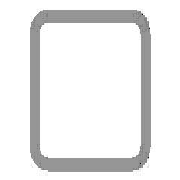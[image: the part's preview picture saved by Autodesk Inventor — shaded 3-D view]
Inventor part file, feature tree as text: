
AUTODESK INVENTOR PART (.ipt)
format: ipt  version: 2025 (Build 290162010, 162A)  size: 133,120 bytes
history: native  units: mm (DEFAULTED — no unit token found)
features: other x4, sketch x1, plane x1
ambient origin geometry x8: Origin, YZ Plane, XZ Plane, XY Plane, X Axis, Y Axis, Z Axis, Center Point
bodies: Solid1 (feature_tree), Body (feature_tree)
feature tree (6):
  parser-record x1  (decoder bookkeeping rows leaked as tree rows — omitted from the tree; the rows remain in map.json)
  other  "Driven Length"
  other  "Start Plane"
  other  "End Plane"
  sketch  "Sketch3"  dims[d3=1405.167342mm d4=0.0mm d7=8.0mm d9=50.0mm d11=50.0mm d12=4.0mm d13=-0.0mm d14=1405.167342mm d15=25.0mm d16=25.0mm d17=90.0deg d18=1405.167342mm]
  plane  "Work Plane3"
